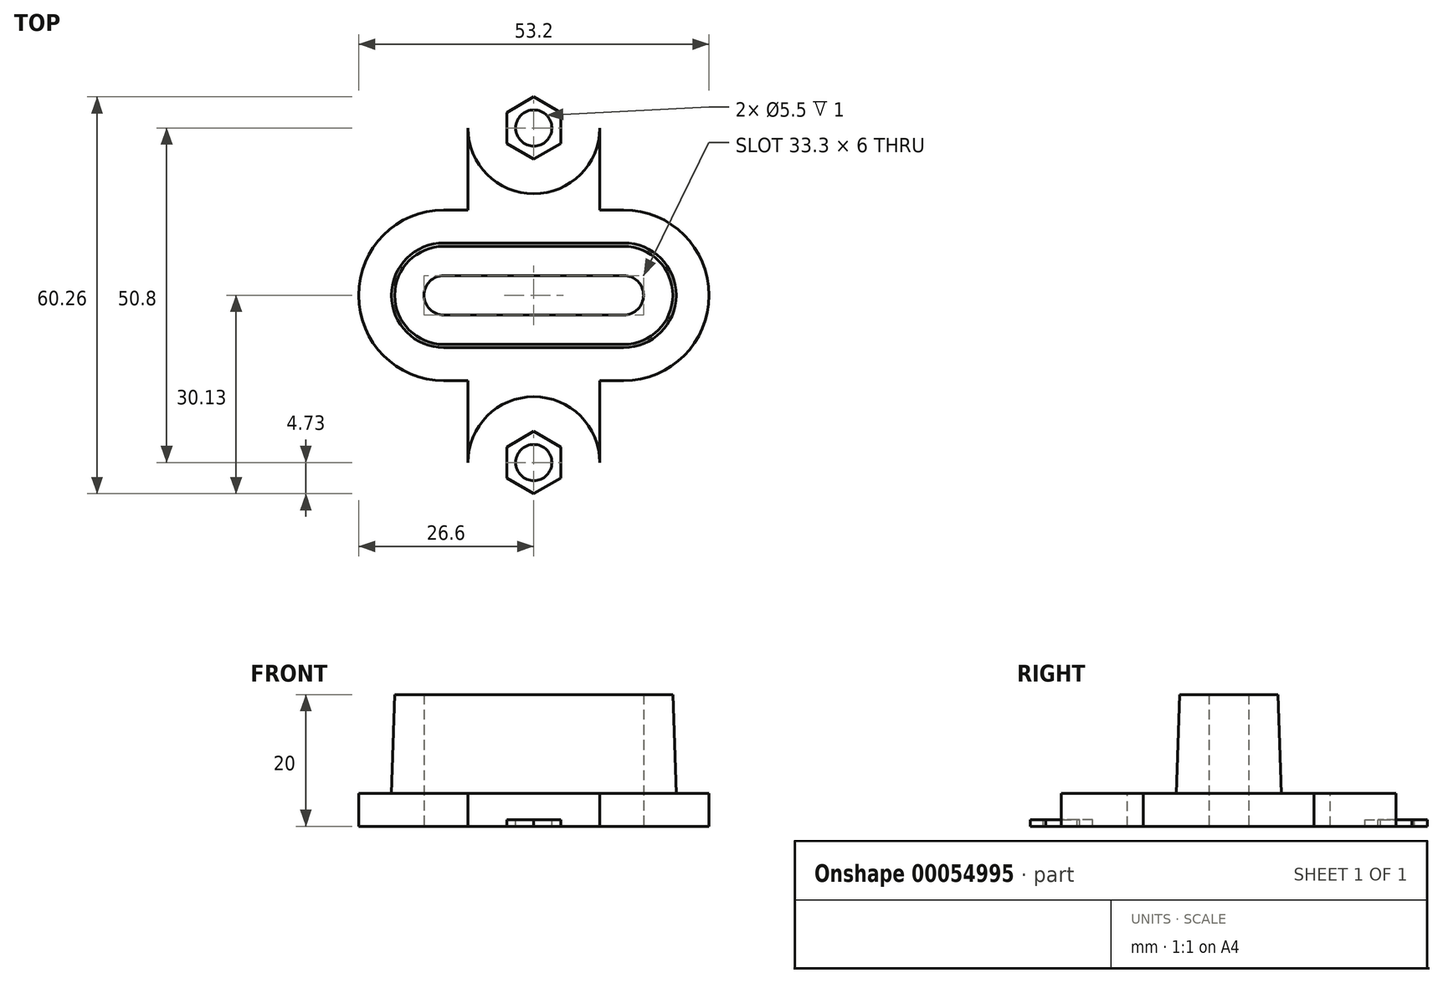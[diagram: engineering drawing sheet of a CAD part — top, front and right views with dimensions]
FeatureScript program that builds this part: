
annotation { "Feature Type Name" : "Feature", "Feature Type Description" : "" }
export const myFeature = defineFeature(function(context is Context, id is Id, definition is map)
    precondition{}
    {
        {
            var Q0;
            Q0=qCreatedBy(makeId("Top.planeOp"),FACE);
            var sketch = newSketch(context, id + "F0", { "sketchPlane" : qUnion([Q0])});
            skLineSegment(sketch, "E0.bottom", {"start": v(-13.65, 7.7) * mm, "end": v(13.65, 7.7) * mm});
            skLineSegment(sketch, "E0.top", {"start": v(-13.65, -7.7) * mm, "end": v(13.65, -7.7) * mm});
            skLineSegment(sketch, "E0.left", {"start": v(-21.35, 0) * mm, "end": v(-21.35, 0) * mm});
            skLineSegment(sketch, "E0.right", {"start": v(21.35, 0) * mm, "end": v(21.35, 0) * mm});
            skPoint(sketch, "E1", {"position": v(0, 7.7) * mm});
            skPoint(sketch, "E2", {"position": v(21.35, 0) * mm});
            skPoint(sketch, "E3.visualSharp", {"position": v(-21.35, 7.7) * mm});
            skArc(sketch, "E3.filletArc", {"start": v(-13.65, 7.7) * mm, "mid": v(-19.1, 5.44) * mm, "end": v(-21.35, 0) * mm});
            skPoint(sketch, "E4.visualSharp", {"position": v(-21.35, -7.7) * mm});
            skArc(sketch, "E4.filletArc", {"start": v(-21.35, 0) * mm, "mid": v(-19.1, -5.44) * mm, "end": v(-13.65, -7.7) * mm});
            skPoint(sketch, "E5.visualSharp", {"position": v(21.35, -7.7) * mm});
            skArc(sketch, "E5.filletArc", {"start": v(13.65, -7.7) * mm, "mid": v(19.1, -5.44) * mm, "end": v(21.35, 0) * mm});
            skPoint(sketch, "E6.visualSharp", {"position": v(21.35, 7.7) * mm});
            skArc(sketch, "E6.filletArc", {"start": v(21.35, 0) * mm, "mid": v(19.1, 5.44) * mm, "end": v(13.65, 7.7) * mm});
            skSolve(sketch);
        }
        {
            var Q0;
            Q0=qCreatedBy(makeId("Top.planeOp"),FACE);
            var sketch = newSketch(context, id + "F1", { "sketchPlane" : qUnion([Q0])});
            skLineSegment(sketch, "E7.bottom", {"start": v(-13.65, 3) * mm, "end": v(13.65, 3) * mm});
            skLineSegment(sketch, "E7.top", {"start": v(-13.65, -3) * mm, "end": v(13.65, -3) * mm});
            skLineSegment(sketch, "E7.left", {"start": v(-16.65, 0) * mm, "end": v(-16.65, 0) * mm});
            skLineSegment(sketch, "E7.right", {"start": v(16.65, 0) * mm, "end": v(16.65, 0) * mm});
            skPoint(sketch, "E8", {"position": v(0, 3) * mm});
            skPoint(sketch, "E9", {"position": v(16.65, 0) * mm});
            skPoint(sketch, "E10.visualSharp", {"position": v(-16.65, 3) * mm});
            skArc(sketch, "E10.filletArc", {"start": v(-13.65, 3) * mm, "mid": v(-15.77, 2.12) * mm, "end": v(-16.65, 0) * mm});
            skPoint(sketch, "E11.visualSharp", {"position": v(-16.65, -3) * mm});
            skArc(sketch, "E11.filletArc", {"start": v(-16.65, 0) * mm, "mid": v(-15.77, -2.12) * mm, "end": v(-13.65, -3) * mm});
            skPoint(sketch, "E12.visualSharp", {"position": v(16.65, -3) * mm});
            skArc(sketch, "E12.filletArc", {"start": v(13.65, -3) * mm, "mid": v(15.77, -2.12) * mm, "end": v(16.65, 0) * mm});
            skPoint(sketch, "E13.visualSharp", {"position": v(16.65, 3) * mm});
            skArc(sketch, "E13.filletArc", {"start": v(16.65, 0) * mm, "mid": v(15.77, 2.12) * mm, "end": v(13.65, 3) * mm});
            skSolve(sketch);
        }
        {
            var Q0;
            Q0=makeQuery(id+"F0.imprint","IMPRINT",FACE,{"disambiguationData":[TD([[makeQuery(id+"F0.imprint","IMPRINT",EDGE,{"derivedFrom":sQuery(id+"F0.wireOp",EDGE,"E0.bottom")}),-1.0]])]});
            extrude(context, id + "F2", {"entities" : qUnion([Q0]), "depth" : 7.5 * mm, "hasDraft" : true, "draftAngle" : 1.9 * degree, "draftPullDirection" : true, "hasSecondDirection" : true, "secondDirectionOppositeDirection" : true, "secondDirectionDepth" : 7.5 * mm, "hasSecondDirectionDraft" : true, "secondDirectionDraftAngle" : 1.9 * degree});
        }
        {
            var Q0;
            Q0=makeQuery(id+"F1.imprint","IMPRINT",FACE,{"disambiguationData":[TD([[makeQuery(id+"F1.imprint","IMPRINT",EDGE,{"derivedFrom":sQuery(id+"F1.wireOp",EDGE,"E7.bottom")}),-1.0]])]});
            var Q1;
            Q1=makeQuery(id+"F2.opExtrude","CAP_FACE",FACE,{"disambiguationData":[OSD([sQuery(id+"F0.wireOp",EDGE,"E0.bottom"),sQuery(id+"F0.wireOp",EDGE,"E0.top"),sQuery(id+"F0.wireOp",EDGE,"E0.left"),sQuery(id+"F0.wireOp",EDGE,"E0.right"),sQuery(id+"F0.wireOp",EDGE,"E3.filletArc"),sQuery(id+"F0.wireOp",EDGE,"E4.filletArc"),sQuery(id+"F0.wireOp",EDGE,"E5.filletArc"),sQuery(id+"F0.wireOp",EDGE,"E6.filletArc")])],"isStart":false});
            var Q2;
            Q2=makeQuery(id+"F2.opExtrude","CAP_FACE",FACE,{"disambiguationData":[OSD([sQuery(id+"F0.wireOp",EDGE,"E0.bottom"),sQuery(id+"F0.wireOp",EDGE,"E0.top"),sQuery(id+"F0.wireOp",EDGE,"E0.left"),sQuery(id+"F0.wireOp",EDGE,"E0.right"),sQuery(id+"F0.wireOp",EDGE,"E3.filletArc"),sQuery(id+"F0.wireOp",EDGE,"E4.filletArc"),sQuery(id+"F0.wireOp",EDGE,"E5.filletArc"),sQuery(id+"F0.wireOp",EDGE,"E6.filletArc")])],"isStart":true});
            extrude(context, id + "F3", {"entities" : qUnion([Q0]), "operationType" : NewBodyOperationType.REMOVE, "endBound" : BoundingType.UP_TO_SURFACE, "endBoundEntityFace" : qUnion([Q1]), "depth" : 10 * mm, "hasSecondDirection" : true, "secondDirectionBound" : SecondDirectionBoundingType.UP_TO_SURFACE, "secondDirectionOppositeDirection" : true, "secondDirectionBoundEntityFace" : qUnion([Q2]), "secondDirectionDepth" : 25 * mm});
        }
        {
            var Q0;
            Q0=makeQuery(id+"F2.opExtrude","CAP_FACE",FACE,{"disambiguationData":[OSD([sQuery(id+"F0.wireOp",EDGE,"E0.bottom"),sQuery(id+"F0.wireOp",EDGE,"E0.top"),sQuery(id+"F0.wireOp",EDGE,"E3.filletArc"),sQuery(id+"F0.wireOp",EDGE,"E4.filletArc"),sQuery(id+"F0.wireOp",EDGE,"E5.filletArc"),sQuery(id+"F0.wireOp",EDGE,"E6.filletArc")])],"isStart":true});
            var sketch = newSketch(context, id + "F4", { "sketchPlane" : qUnion([Q0])});
            skLineSegment(sketch, "E14", {"start": v(0, 0) * mm, "end": v(25.4, 0) * mm, "construction": true});
            skLineSegment(sketch, "E15", {"start": v(25.4, 0) * mm, "end": v(50.8, 0) * mm, "construction": true});
            skLineSegment(sketch, "E16", {"start": v(0, 0) * mm, "end": v(-25.4, 0) * mm, "construction": true});
            skLineSegment(sketch, "E17", {"start": v(-25.4, 0) * mm, "end": v(-50.8, 0) * mm, "construction": true});
            skLineSegment(sketch, "E18", {"start": v(0, 0) * mm, "end": v(0, 25.4) * mm, "construction": true});
            skLineSegment(sketch, "E19", {"start": v(0, 25.4) * mm, "end": v(0, 50.8) * mm, "construction": true});
            skLineSegment(sketch, "E20", {"start": v(0, 0) * mm, "end": v(0, -25.4) * mm, "construction": true});
            skLineSegment(sketch, "E21", {"start": v(0, -25.4) * mm, "end": v(0, -50.8) * mm, "construction": true});
            skLineSegment(sketch, "E22.0.0", {"start": v(-13.65, -7.95) * mm, "end": v(13.65, -7.95) * mm});
            skLineSegment(sketch, "E22.0.1", {"start": v(13.65, -7.95) * mm, "end": v(13.65, -7.95) * mm});
            skLineSegment(sketch, "E22.0.4", {"start": v(-13.65, 7.95) * mm, "end": v(13.65, 7.95) * mm});
            skLineSegment(sketch, "E22.0.5", {"start": v(-13.65, 7.95) * mm, "end": v(-13.65, 7.95) * mm});
            skLineSegment(sketch, "E23.0", {"start": v(-13.65, 12.95) * mm, "end": v(13.65, 12.95) * mm});
            skArc(sketch, "E23.1", {"start": v(26.6, -0.23) * mm, "mid": v(22.89, 9.08) * mm, "end": v(13.65, 12.95) * mm});
            skLineSegment(sketch, "E23.2", {"start": v(26.6, -0.23) * mm, "end": v(26.6, -0.23) * mm});
            skArc(sketch, "E23.3", {"start": v(13.65, -12.95) * mm, "mid": v(22.73, -9.24) * mm, "end": v(26.6, -0.23) * mm});
            skLineSegment(sketch, "E23.4", {"start": v(-13.65, -12.95) * mm, "end": v(13.65, -12.95) * mm});
            skArc(sketch, "E23.5", {"start": v(-13.65, 12.95) * mm, "mid": v(-22.73, 9.24) * mm, "end": v(-26.6, 0.23) * mm});
            skArc(sketch, "E23.6", {"start": v(-26.6, 0.23) * mm, "mid": v(-22.89, -9.08) * mm, "end": v(-13.65, -12.95) * mm});
            skLineSegment(sketch, "E23.7", {"start": v(-26.6, 0.23) * mm, "end": v(-26.6, 0.23) * mm});
            skCircle(sketch, "E24", {"center": v(0, -25.4) * mm, "radius": 10 * mm});
            skCircle(sketch, "E25", {"center": v(0, 25.4) * mm, "radius": 10 * mm});
            skLineSegment(sketch, "E26", {"start": v(-10, -12.95) * mm, "end": v(-10, -25.4) * mm});
            skLineSegment(sketch, "E27", {"start": v(10, -12.95) * mm, "end": v(10, -25.4) * mm});
            skLineSegment(sketch, "E28", {"start": v(-10, 12.95) * mm, "end": v(-10, 25.4) * mm});
            skLineSegment(sketch, "E29", {"start": v(10, 12.95) * mm, "end": v(10, 25.4) * mm});
            skCircle(sketch, "E30", {"center": v(0, -25.4) * mm, "radius": 2.75 * mm});
            skCircle(sketch, "E31", {"center": v(0, 25.4) * mm, "radius": 2.75 * mm});
            skCircle(sketch, "E32.cCircle", {"center": v(0, 25.4) * mm, "radius": 4.1 * mm, "construction": true});
            skLineSegment(sketch, "E32.0", {"start": v(4.1, 27.77) * mm, "end": v(4.1, 23.03) * mm});
            skLineSegment(sketch, "E32.1", {"start": v(4.1, 23.03) * mm, "end": v(0, 20.67) * mm});
            skLineSegment(sketch, "E32.2", {"start": v(0, 20.67) * mm, "end": v(-4.1, 23.03) * mm});
            skLineSegment(sketch, "E32.3", {"start": v(-4.1, 23.03) * mm, "end": v(-4.1, 27.77) * mm});
            skLineSegment(sketch, "E32.4", {"start": v(-4.1, 27.77) * mm, "end": v(0, 30.13) * mm});
            skLineSegment(sketch, "E32.5", {"start": v(0, 30.13) * mm, "end": v(4.1, 27.77) * mm});
            skPoint(sketch, "E32.0.midPoint", {"position": v(4.1, 25.4) * mm});
            skLineSegment(sketch, "E33", {"start": v(0, 25.4) * mm, "end": v(4.1, 25.4) * mm, "construction": true});
            skLineSegment(sketch, "E34.5", {"start": v(0, -20.67) * mm, "end": v(4.1, -23.03) * mm});
            skCircle(sketch, "E34.cCircle", {"center": v(0, -25.4) * mm, "radius": 4.1 * mm, "construction": true});
            skLineSegment(sketch, "E35", {"start": v(0, -25.4) * mm, "end": v(4.1, -25.4) * mm, "construction": true});
            skLineSegment(sketch, "E34.0", {"start": v(4.1, -23.03) * mm, "end": v(4.1, -27.77) * mm});
            skLineSegment(sketch, "E34.4", {"start": v(-4.1, -23.03) * mm, "end": v(0, -20.67) * mm});
            skLineSegment(sketch, "E34.3", {"start": v(-4.1, -27.77) * mm, "end": v(-4.1, -23.03) * mm});
            skLineSegment(sketch, "E34.2", {"start": v(0, -30.13) * mm, "end": v(-4.1, -27.77) * mm});
            skPoint(sketch, "E34.0.midPoint", {"position": v(4.1, -25.4) * mm});
            skLineSegment(sketch, "E34.1", {"start": v(4.1, -27.77) * mm, "end": v(0, -30.13) * mm});
            skSolve(sketch);
        }
        {
            var Q0;
            Q0=makeQuery(id+"F4.imprint","IMPRINT",FACE,{"disambiguationData":[TD([[makeQuery(id+"F4.imprint","IMPRINT",EDGE,{"derivedFrom":sQuery(id+"F4.wireOp",EDGE,"E22.0.0")}),1.0]])]});
            var Q1;
            Q1=makeQuery(id+"F4.imprint","IMPRINT",FACE,{"disambiguationData":[TD([[makeQuery(id+"F4.imprint","IMPRINT",EDGE,{"derivedFrom":sQuery(id+"F4.wireOp",EDGE,"E22.0.0")}),-1.0]])]});
            var Q2;
            {var subQ0=sQuery(id+"F4.wireOp",EDGE,"E25");var subQ1=sQuery(id+"F4.wireOp",EDGE,"E23.0");var subQ4=makeQuery(id+"F4.imprint","INTERSECT",VERTEX,{"disambiguationData":[OD(0.0)],"derivedFrom":[subQ1,subQ0]});Q2=makeQuery(id+"F4.imprint","IMPRINT",FACE,{"disambiguationData":[TD([[makeQuery(id+"F4.imprint","IMPRINT",EDGE,{"disambiguationData":[TD([[subQ4,-1.0]])],"derivedFrom":subQ1}),1.0]])]});}
            var Q3;
            {var subQ0=sQuery(id+"F4.wireOp",EDGE,"E28");Q3=makeQuery(id+"F4.imprint","IMPRINT",FACE,{"disambiguationData":[TD([[makeQuery(id+"F4.imprint","IMPRINT",EDGE,{"derivedFrom":subQ0}),-1.0]])]});}
            var Q4;
            {var subQ0=sQuery(id+"F4.wireOp",EDGE,"E25");var subQ1=sQuery(id+"F4.wireOp",EDGE,"E23.0");var subQ3=makeQuery(id+"F4.imprint","INTERSECT",VERTEX,{"disambiguationData":[OD(0.0)],"derivedFrom":[subQ1,subQ0]});Q4=makeQuery(id+"F4.imprint","IMPRINT",FACE,{"disambiguationData":[TD([[makeQuery(id+"F4.imprint","IMPRINT",EDGE,{"disambiguationData":[TD([[subQ3,-1.0]])],"derivedFrom":subQ1}),-1.0]])]});}
            var Q5;
            {var subQ0=sQuery(id+"F4.wireOp",EDGE,"E29");Q5=makeQuery(id+"F4.imprint","IMPRINT",FACE,{"disambiguationData":[TD([[makeQuery(id+"F4.imprint","IMPRINT",EDGE,{"derivedFrom":subQ0}),1.0]])]});}
            var Q6;
            {var subQ0=sQuery(id+"F4.wireOp",EDGE,"E24");var subQ1=sQuery(id+"F4.wireOp",EDGE,"E23.4");var subQ3=makeQuery(id+"F4.imprint","INTERSECT",VERTEX,{"disambiguationData":[OD(0.0)],"derivedFrom":[subQ1,subQ0]});Q6=makeQuery(id+"F4.imprint","IMPRINT",FACE,{"disambiguationData":[TD([[makeQuery(id+"F4.imprint","IMPRINT",EDGE,{"disambiguationData":[TD([[subQ3,-1.0]])],"derivedFrom":subQ1}),1.0]])]});}
            var Q7;
            {var subQ0=sQuery(id+"F4.wireOp",EDGE,"E26");Q7=makeQuery(id+"F4.imprint","IMPRINT",FACE,{"disambiguationData":[TD([[makeQuery(id+"F4.imprint","IMPRINT",EDGE,{"derivedFrom":subQ0}),1.0]])]});}
            var Q8;
            {var subQ0=sQuery(id+"F4.wireOp",EDGE,"E24");var subQ3=sQuery(id+"F4.wireOp",EDGE,"E23.4");var subQ4=makeQuery(id+"F4.imprint","INTERSECT",VERTEX,{"disambiguationData":[OD(0.0)],"derivedFrom":[subQ3,subQ0]});Q8=makeQuery(id+"F4.imprint","IMPRINT",FACE,{"disambiguationData":[TD([[makeQuery(id+"F4.imprint","IMPRINT",EDGE,{"disambiguationData":[TD([[subQ4,-1.0]])],"derivedFrom":subQ3}),-1.0]])]});}
            var Q9;
            {var subQ0=sQuery(id+"F4.wireOp",EDGE,"E27");Q9=makeQuery(id+"F4.imprint","IMPRINT",FACE,{"disambiguationData":[TD([[makeQuery(id+"F4.imprint","IMPRINT",EDGE,{"derivedFrom":subQ0}),-1.0]])]});}
            var Q10;
            Q10=makeQuery(id+"F4.imprint","IMPRINT",FACE,{"disambiguationData":[TD([[makeQuery(id+"F4.imprint","IMPRINT",EDGE,{"derivedFrom":sQuery(id+"F4.wireOp",EDGE,"E30")}),-1.0]])]});
            var Q11;
            Q11=makeQuery(id+"F4.imprint","IMPRINT",FACE,{"disambiguationData":[TD([[makeQuery(id+"F4.imprint","IMPRINT",EDGE,{"derivedFrom":sQuery(id+"F4.wireOp",EDGE,"E31")}),-1.0]])]});
            extrude(context, id + "F5", {"entities" : qUnion([Q0, Q1, Q2, Q3, Q4, Q5, Q6, Q7, Q8, Q9, Q10, Q11]), "operationType" : NewBodyOperationType.ADD, "depth" : 5 * mm});
        }
        {
            var Q0;
            Q0=makeQuery(id+"F4.imprint","IMPRINT",FACE,{"disambiguationData":[TD([[makeQuery(id+"F4.imprint","IMPRINT",EDGE,{"derivedFrom":sQuery(id+"F4.wireOp",EDGE,"E31")}),-1.0]])]});
            var Q1;
            Q1=makeQuery(id+"F4.imprint","IMPRINT",FACE,{"disambiguationData":[TD([[makeQuery(id+"F4.imprint","IMPRINT",EDGE,{"derivedFrom":sQuery(id+"F4.wireOp",EDGE,"E30")}),-1.0]])]});
            extrude(context, id + "F6", {"entities" : qUnion([Q0, Q1]), "operationType" : NewBodyOperationType.REMOVE, "depth" : 4 * mm});
        }
    });
